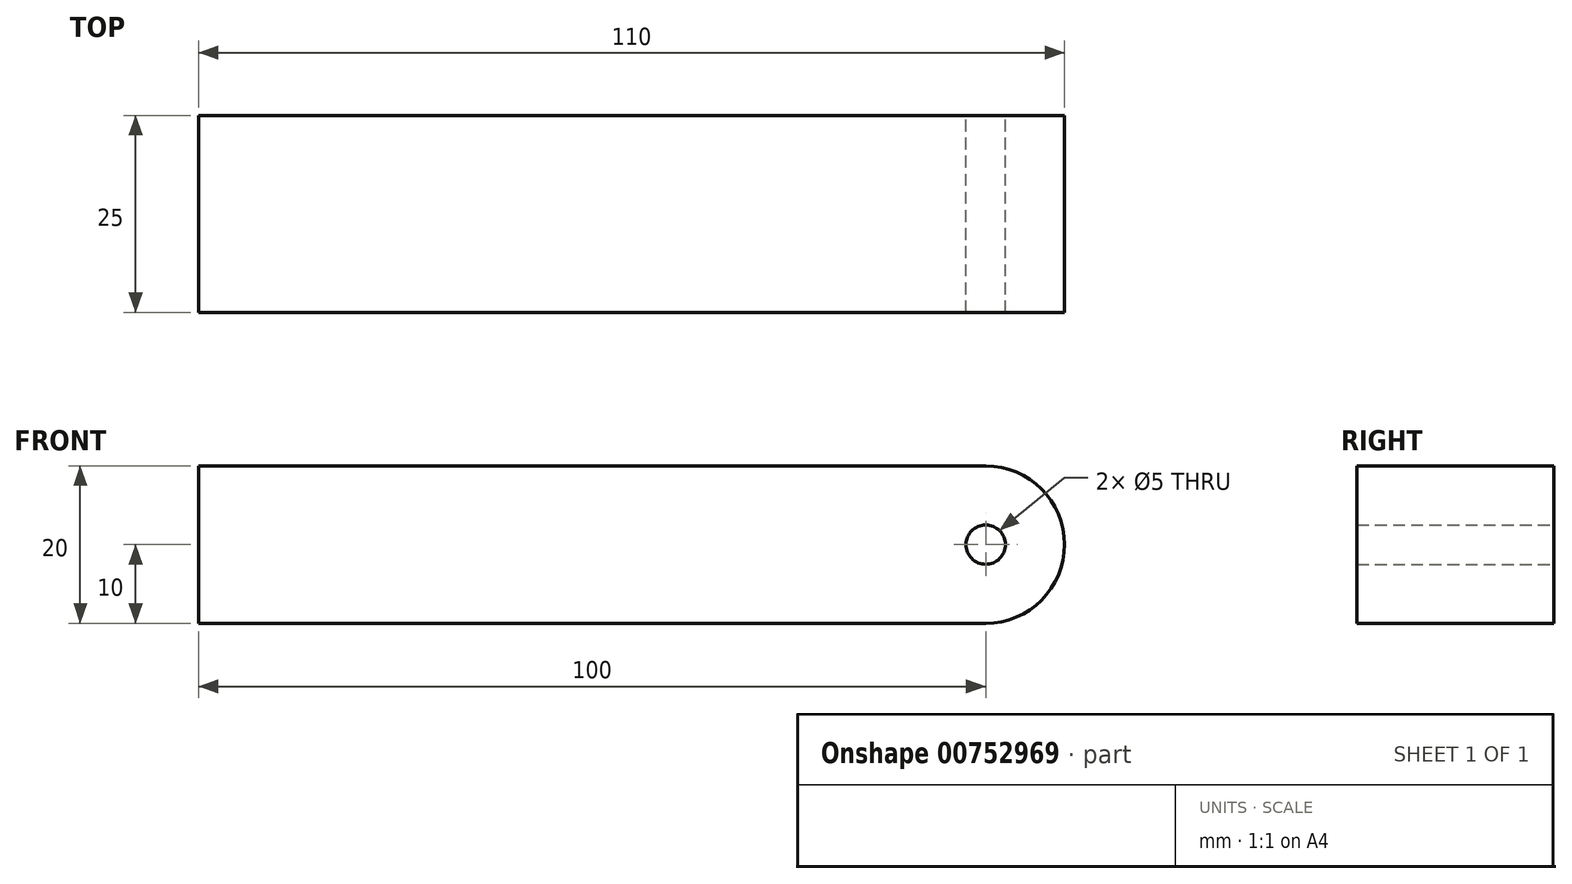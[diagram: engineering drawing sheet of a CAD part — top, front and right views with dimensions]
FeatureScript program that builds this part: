
annotation { "Feature Type Name" : "Feature", "Feature Type Description" : "" }
export const myFeature = defineFeature(function(context is Context, id is Id, definition is map)
    precondition{}
    {
        {
            var Q0;
            Q0=qCreatedBy(makeId("Front.planeOp"),FACE);
            var sketch = newSketch(context, id + "F0", { "sketchPlane" : qUnion([Q0])});
            skLineSegment(sketch, "E0.bottom", {"start": v(50, -10) * mm, "end": v(-50, -10) * mm});
            skLineSegment(sketch, "E0.top", {"start": v(50, 10) * mm, "end": v(-50, 10) * mm});
            skLineSegment(sketch, "E0.left", {"start": v(50, -10) * mm, "end": v(50, 10) * mm, "construction": true});
            skLineSegment(sketch, "E0.right", {"start": v(-50, -10) * mm, "end": v(-50, 10) * mm});
            skPoint(sketch, "E0.middle", {"position": v(0, 0) * mm});
            skArc(sketch, "E1", {"start": v(50, 10) * mm, "mid": v(60, 0) * mm, "end": v(50, -10) * mm});
            skCircle(sketch, "E2", {"center": v(50, 0) * mm, "radius": 2.5 * mm});
            skSolve(sketch);
        }
        {
            var Q0;
            Q0 = qSketchRegion(id + "F0", true);
            extrude(context, id + "F1", {"entities" : qUnion([Q0]), "depth" : 25 * mm, "offsetDistance" : 25 * mm});
        }
    });
